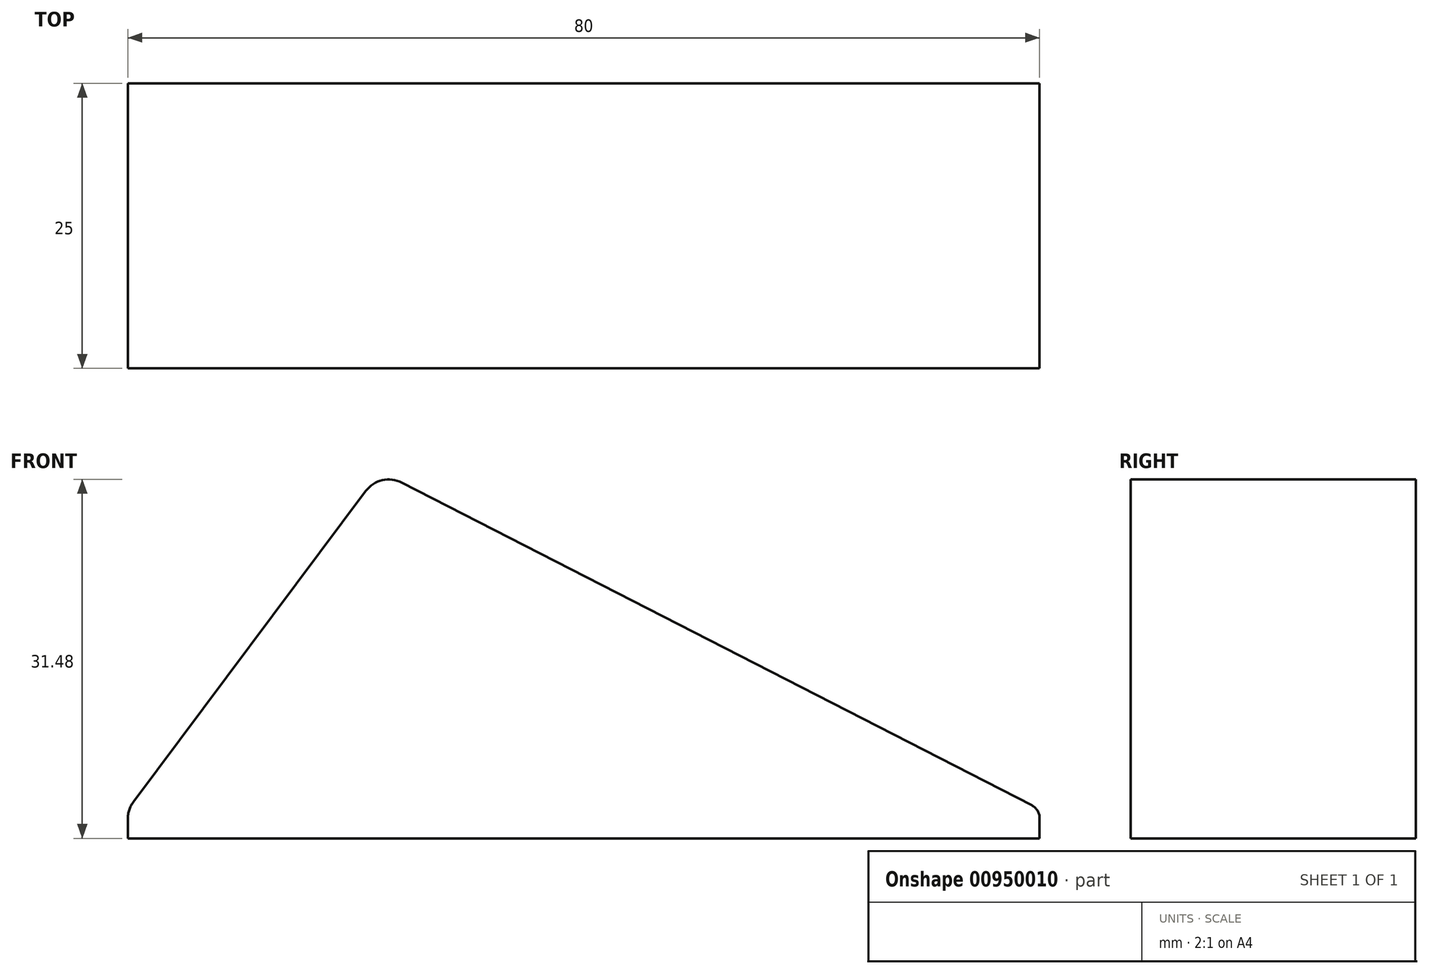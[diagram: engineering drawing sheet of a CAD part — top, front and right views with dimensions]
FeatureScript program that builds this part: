
annotation { "Feature Type Name" : "Feature", "Feature Type Description" : "" }
export const myFeature = defineFeature(function(context is Context, id is Id, definition is map)
    precondition{}
    {
        {
            var Q0;
            Q0=qCreatedBy(makeId("Front.planeOp"),FACE);
            var sketch = newSketch(context, id + "F0", { "sketchPlane" : qUnion([Q0])});
            skLineSegment(sketch, "E0", {"start": v(-24.9, 0) * mm, "end": v(55.1, 0) * mm});
            skLineSegment(sketch, "E1", {"start": v(-24.9, 0) * mm, "end": v(-2.76, 29.64) * mm});
            skLineSegment(sketch, "E2", {"start": v(-2.76, 29.64) * mm, "end": v(55.1, 0) * mm});
            skSolve(sketch);
        }
        {
            var Q0;
            Q0=makeQuery(id+"F0.imprint","IMPRINT",FACE,{"disambiguationData":[TD([[makeQuery(id+"F0.imprint","IMPRINT",EDGE,{"derivedFrom":sQuery(id+"F0.wireOp",EDGE,"E0")}),1.0]])]});
            extrude(context, id + "F1", {"entities" : qUnion([Q0]), "depth" : 25 * mm, "offsetDistance" : 25.4 * mm});
        }
        {
            var Q0;
            Q0=makeQuery(id+"F1.opExtrude","SWEPT_EDGE",EDGE,{"disambiguationData":[OSD([sQuery(id+"F0.wireOp",EDGE,"E1"),sQuery(id+"F0.wireOp",EDGE,"E2")])]});
            fillet(context, id + "F2", {"entities" : qUnion([Q0]), "radius" : 2.54 * mm, "tangentPropagation" : true, "allowEdgeOverflow" : false});
        }
        {
            var Q0;
            Q0=makeQuery(id+"F1.opExtrude","SWEPT_FACE",FACE,{"disambiguationData":[OSD([sQuery(id+"F0.wireOp",EDGE,"E0")])]});
            extrude(context, id + "F3", {"entities" : qUnion([Q0]), "operationType" : NewBodyOperationType.ADD, "depth" : 2.54 * mm, "offsetDistance" : 25.4 * mm});
        }
        {
            var Q0;
            {var subQ0=sQuery(id+"F0.wireOp",EDGE,"E1");var subQ1=sQuery(id+"F0.wireOp",EDGE,"E0");Q0=makeQuery(id+"F3.boolean.opBoolean","MERGE",EDGE,{"derivedFrom":[makeQuery(id+"F1.opExtrude","SWEPT_EDGE",EDGE,{"disambiguationData":[OSD([subQ1,subQ0])]}),makeQuery(id+"F3.opExtrude","CAP_EDGE",EDGE,{"disambiguationData":[OSD([subQ1,subQ0])],"isStart":true})]});}
            fillet(context, id + "F4", {"entities" : qUnion([Q0]), "radius" : 2.54 * mm, "tangentPropagation" : true, "allowEdgeOverflow" : false});
        }
        {
            var Q0;
            {var subQ0=sQuery(id+"F0.wireOp",EDGE,"E2");var subQ1=sQuery(id+"F0.wireOp",EDGE,"E0");Q0=makeQuery(id+"F3.boolean.opBoolean","MERGE",EDGE,{"derivedFrom":[makeQuery(id+"F1.opExtrude","SWEPT_EDGE",EDGE,{"disambiguationData":[OSD([subQ1,subQ0])]}),makeQuery(id+"F3.opExtrude","CAP_EDGE",EDGE,{"disambiguationData":[OSD([subQ1,subQ0])],"isStart":true})]});}
            fillet(context, id + "F5", {"entities" : qUnion([Q0]), "radius" : 1.27 * mm, "tangentPropagation" : true, "allowEdgeOverflow" : false});
        }
    });
